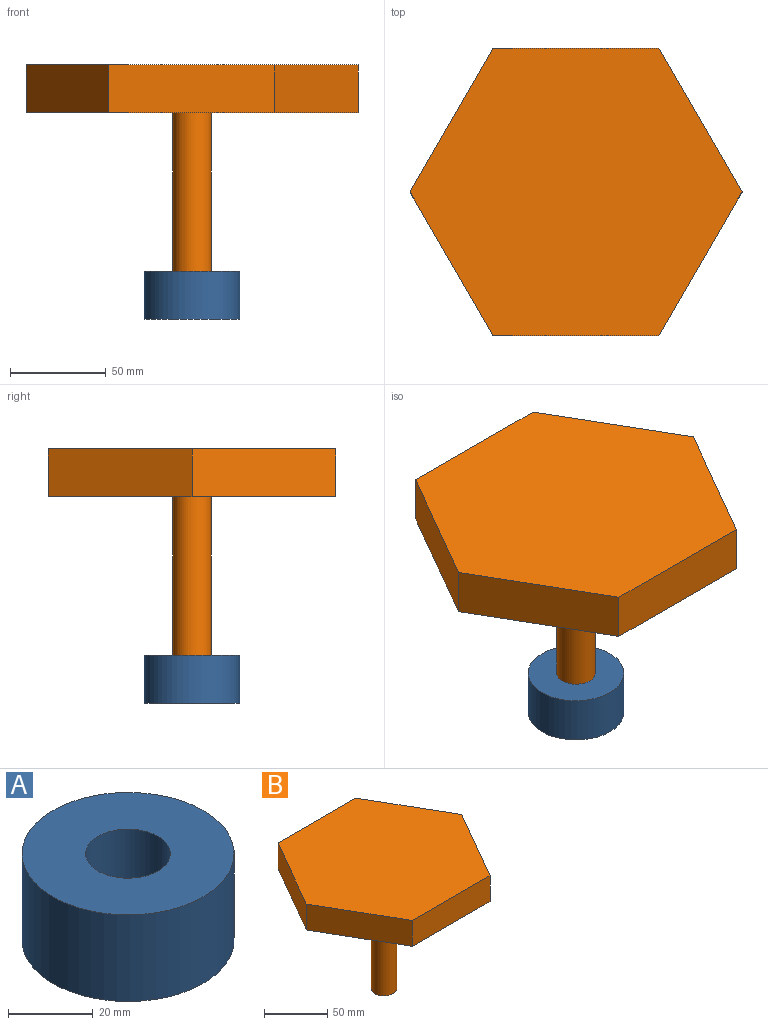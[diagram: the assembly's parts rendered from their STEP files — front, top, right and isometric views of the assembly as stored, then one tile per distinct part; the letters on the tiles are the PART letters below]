
ASSEMBLY  parts=2 mates=1
PART A: 5 faces, bbox 50x50x25 mm
  f0: cylinder r=10mm len=20mm, axis (0,0,-1), area 1256.6mm2, adj f2,f4
  f1: cylinder r=25mm len=50mm, axis (0,0,-1), area 3927mm2, adj f2,f3
  f2: plane 50x50mm, normal (0,0,1), area 1649.3mm2, adj f0,f1
  f3: plane 50x50mm, normal (0,0,-1), area 1963.5mm2, adj f1
  f4: plane 20x20mm, normal (0,0,1), area 314.2mm2, adj f0
PART B: 10 faces, bbox 173.2x150x125 mm
  f0: plane 86.6x25mm, normal (0,1,0), area 2165.1mm2, adj f1,f5,f6,f7
  f1: plane 75x43.3mm, normal (-0.87,0.5,0), area 2165.1mm2, adj f0,f2,f6,f7
  f2: plane 75x43.3mm, normal (-0.87,-0.5,0), area 2165.1mm2, adj f1,f3,f6,f7
  f3: plane 86.6x25mm, normal (0,-1,0), area 2165.1mm2, adj f2,f4,f6,f7
  f4: plane 75x43.3mm, normal (0.87,-0.5,0), area 2165.1mm2, adj f3,f5,f6,f7
  f5: plane 75x43.3mm, normal (0.87,0.5,0), area 2165.1mm2, adj f0,f4,f6,f7
  f6: plane 173.21x150mm, normal (0,0,1), area 19485.6mm2, adj f0,f1,f2,f3,f4,f5
  f7: plane 173.21x150mm, normal (0,0,-1), area 19171.4mm2, adj f0,f1,f2,f3,f4,f5,f8
  f8: cylinder r=10mm len=100mm, axis (0,0,1), area 6283.2mm2, adj f7,f9
  f9: plane 20x20mm, normal (0,0,-1), area 314.2mm2, adj f8
PLACE A t=(17.59,26.26,-3.06)mm fixed
PLACE B t=(17.59,26.26,104.59)mm
MATE slider B.f8 <-> A.f0  axis (0,0,-1) through (17.59,26.26,4.59)mm
